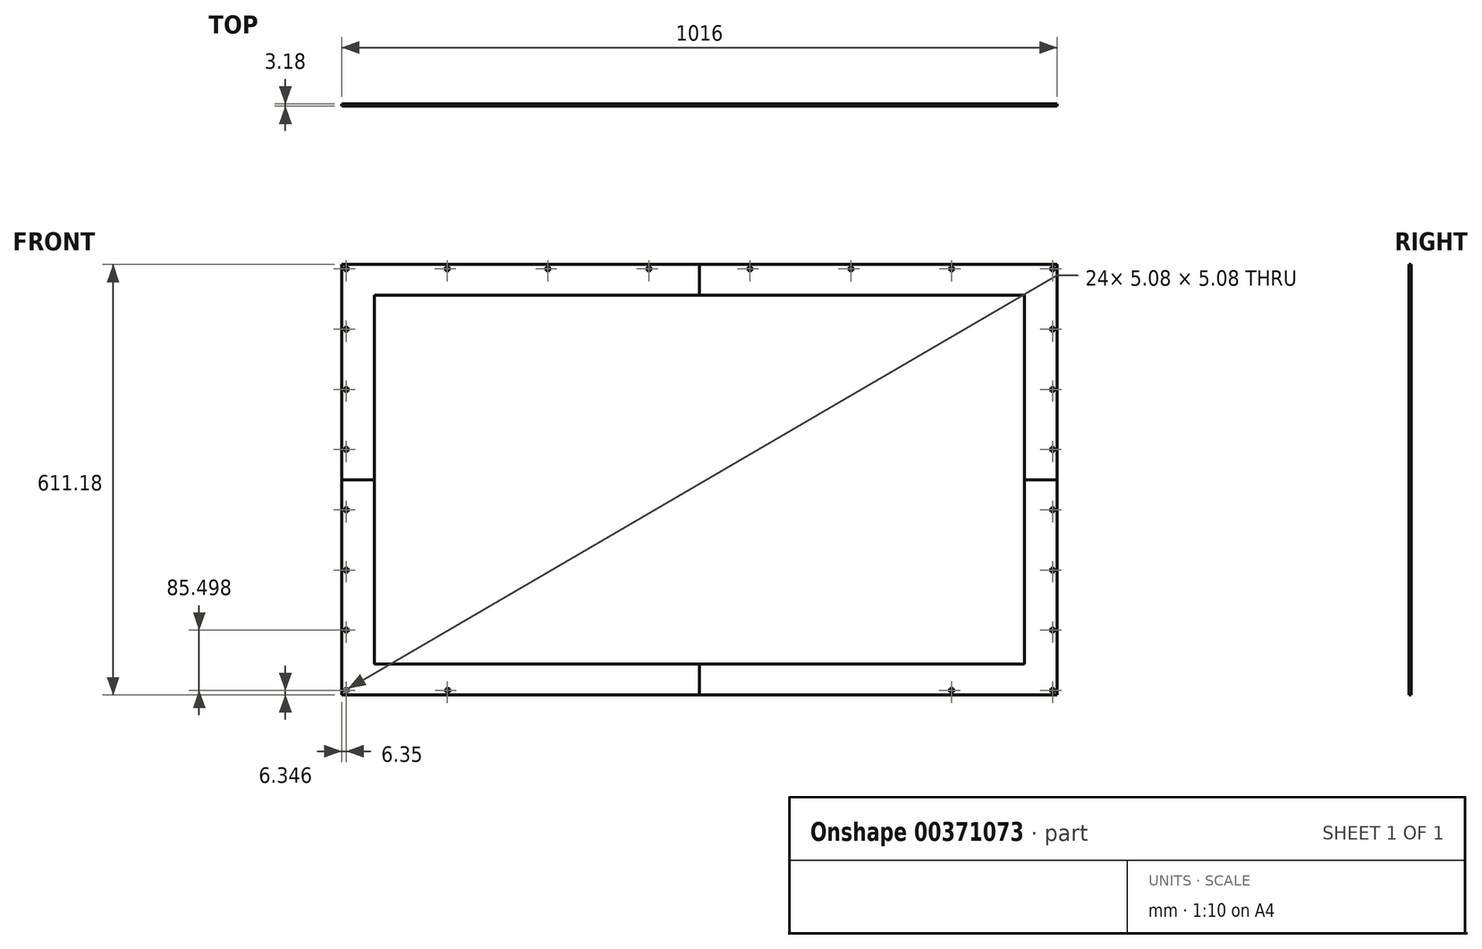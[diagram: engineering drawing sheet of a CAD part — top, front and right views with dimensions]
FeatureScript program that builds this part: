
annotation { "Feature Type Name" : "Feature", "Feature Type Description" : "" }
export const myFeature = defineFeature(function(context is Context, id is Id, definition is map)
    precondition{}
    {
        {
            var Q0;
            Q0=qCreatedBy(makeId("Front.planeOp"),FACE);
            var sketch = newSketch(context, id + "F0", { "sketchPlane" : qUnion([Q0])});
            skLineSegment(sketch, "E0.bottom", {"start": v(495.3, 292.9) * mm, "end": v(-495.3, 292.9) * mm});
            skLineSegment(sketch, "E0.top", {"start": v(495.3, -292.9) * mm, "end": v(-495.3, -292.9) * mm});
            skLineSegment(sketch, "E0.left", {"start": v(495.3, 292.9) * mm, "end": v(495.3, -292.9) * mm});
            skLineSegment(sketch, "E0.right", {"start": v(-495.3, 292.9) * mm, "end": v(-495.3, -292.9) * mm});
            skPoint(sketch, "E0.middle", {"position": v(0, 0) * mm});
            skLineSegment(sketch, "E1.0", {"start": v(-508, 305.6) * mm, "end": v(-508, -305.6) * mm});
            skLineSegment(sketch, "E1.1", {"start": v(508, 305.6) * mm, "end": v(-508, 305.6) * mm});
            skLineSegment(sketch, "E1.2", {"start": v(508, 305.6) * mm, "end": v(508, -305.6) * mm});
            skLineSegment(sketch, "E1.3", {"start": v(508, -305.6) * mm, "end": v(-508, -305.6) * mm});
            skLineSegment(sketch, "E2.bottom", {"start": v(-476, 276.23) * mm, "end": v(476, 276.23) * mm});
            skLineSegment(sketch, "E2.top", {"start": v(-476, -276.23) * mm, "end": v(476, -276.23) * mm});
            skLineSegment(sketch, "E2.left", {"start": v(-476, 276.23) * mm, "end": v(-476, -276.23) * mm});
            skLineSegment(sketch, "E2.right", {"start": v(476, 276.22) * mm, "end": v(476, -276.23) * mm});
            skLineSegment(sketch, "E3.bottom", {"start": v(-355.3, -296.7) * mm, "end": v(-360.38, -296.7) * mm});
            skLineSegment(sketch, "E3.top", {"start": v(-355.3, -301.78) * mm, "end": v(-360.38, -301.78) * mm});
            skLineSegment(sketch, "E3.left", {"start": v(-355.3, -296.7) * mm, "end": v(-355.3, -301.78) * mm});
            skLineSegment(sketch, "E3.right", {"start": v(-360.38, -296.7) * mm, "end": v(-360.38, -301.78) * mm});
            skPoint(sketch, "E3.middle", {"position": v(-357.84, -299.24) * mm});
            skLineSegment(sketch, "E4.MirrorCS", {"start": v(360.38, -296.7) * mm, "end": v(360.38, -301.78) * mm});
            skLineSegment(sketch, "E5.MirrorCS", {"start": v(355.3, -296.7) * mm, "end": v(360.38, -296.7) * mm});
            skLineSegment(sketch, "E6.MirrorCS", {"start": v(355.3, -296.7) * mm, "end": v(355.3, -301.78) * mm});
            skLineSegment(sketch, "E7.MirrorCS", {"start": v(355.3, -301.78) * mm, "end": v(360.38, -301.78) * mm});
            skLineSegment(sketch, "E8.bottom", {"start": v(461.7, 261.93) * mm, "end": v(-461.7, 261.93) * mm});
            skLineSegment(sketch, "E8.top", {"start": v(461.7, -261.93) * mm, "end": v(-461.7, -261.93) * mm});
            skLineSegment(sketch, "E8.left", {"start": v(461.7, 261.93) * mm, "end": v(461.7, -261.93) * mm});
            skLineSegment(sketch, "E8.right", {"start": v(-461.7, 261.93) * mm, "end": v(-461.7, -261.93) * mm});
            skLineSegment(sketch, "E9", {"start": v(-495.3, 292.9) * mm, "end": v(-508, 305.6) * mm});
            skPoint(sketch, "E10", {"position": v(-501.65, 299.24) * mm});
            skLineSegment(sketch, "E11", {"start": v(-495.3, -292.9) * mm, "end": v(-508, -305.6) * mm});
            skPoint(sketch, "E12", {"position": v(-501.65, -299.24) * mm});
            skLineSegment(sketch, "E13", {"start": v(495.3, -292.9) * mm, "end": v(508, -305.6) * mm});
            skPoint(sketch, "E14", {"position": v(501.65, -299.24) * mm});
            skLineSegment(sketch, "E15", {"start": v(495.3, 292.9) * mm, "end": v(508, 305.6) * mm});
            skPoint(sketch, "E16", {"position": v(501.65, 299.24) * mm});
            skPoint(sketch, "E17", {"position": v(-501.65, 213.75) * mm});
            skPoint(sketch, "E18", {"position": v(-501.65, 128.25) * mm});
            skPoint(sketch, "E19", {"position": v(-501.65, 42.75) * mm});
            skPoint(sketch, "E20", {"position": v(-501.65, -42.75) * mm});
            skPoint(sketch, "E21", {"position": v(-501.65, -128.25) * mm});
            skPoint(sketch, "E22", {"position": v(-501.65, -213.75) * mm});
            skLineSegment(sketch, "E23", {"start": v(-501.65, 299.24) * mm, "end": v(-501.65, 213.75) * mm});
            skLineSegment(sketch, "E24", {"start": v(-501.65, 213.75) * mm, "end": v(-501.65, 128.25) * mm});
            skLineSegment(sketch, "E25", {"start": v(-501.65, 128.25) * mm, "end": v(-501.65, 42.75) * mm});
            skLineSegment(sketch, "E26", {"start": v(-501.65, 42.75) * mm, "end": v(-501.65, -42.75) * mm});
            skLineSegment(sketch, "E27", {"start": v(-501.65, -42.75) * mm, "end": v(-501.65, -128.25) * mm});
            skLineSegment(sketch, "E28", {"start": v(-501.65, -128.25) * mm, "end": v(-501.65, -213.75) * mm});
            skLineSegment(sketch, "E29", {"start": v(-501.65, -213.75) * mm, "end": v(-501.65, -299.24) * mm});
            skLineSegment(sketch, "E30.bottom", {"start": v(-499.11, 301.78) * mm, "end": v(-504.2, 301.78) * mm});
            skLineSegment(sketch, "E30.top", {"start": v(-499.11, 296.7) * mm, "end": v(-504.2, 296.7) * mm});
            skLineSegment(sketch, "E30.left", {"start": v(-499.11, 301.78) * mm, "end": v(-499.11, 296.7) * mm});
            skLineSegment(sketch, "E30.right", {"start": v(-504.2, 301.78) * mm, "end": v(-504.2, 296.7) * mm});
            skLineSegment(sketch, "E31.bottom", {"start": v(-499.11, 216.29) * mm, "end": v(-504.2, 216.29) * mm});
            skLineSegment(sketch, "E31.top", {"start": v(-499.11, 211.2) * mm, "end": v(-504.2, 211.2) * mm});
            skLineSegment(sketch, "E31.left", {"start": v(-499.11, 216.29) * mm, "end": v(-499.11, 211.2) * mm});
            skLineSegment(sketch, "E31.right", {"start": v(-504.2, 216.29) * mm, "end": v(-504.2, 211.2) * mm});
            skLineSegment(sketch, "E32.bottom", {"start": v(-499.11, 130.79) * mm, "end": v(-504.2, 130.79) * mm});
            skLineSegment(sketch, "E32.top", {"start": v(-499.11, 125.7) * mm, "end": v(-504.2, 125.7) * mm});
            skLineSegment(sketch, "E32.left", {"start": v(-499.11, 130.79) * mm, "end": v(-499.11, 125.7) * mm});
            skLineSegment(sketch, "E32.right", {"start": v(-504.2, 130.79) * mm, "end": v(-504.2, 125.7) * mm});
            skLineSegment(sketch, "E33.bottom", {"start": v(-499.11, 45.29) * mm, "end": v(-504.2, 45.29) * mm});
            skLineSegment(sketch, "E33.top", {"start": v(-499.11, 40.2) * mm, "end": v(-504.2, 40.2) * mm});
            skLineSegment(sketch, "E33.left", {"start": v(-499.11, 45.29) * mm, "end": v(-499.11, 40.2) * mm});
            skLineSegment(sketch, "E33.right", {"start": v(-504.2, 45.29) * mm, "end": v(-504.2, 40.2) * mm});
            skLineSegment(sketch, "E34.bottom", {"start": v(-499.1, -40.2) * mm, "end": v(-504.19, -40.2) * mm});
            skLineSegment(sketch, "E34.top", {"start": v(-499.1, -45.29) * mm, "end": v(-504.19, -45.29) * mm});
            skLineSegment(sketch, "E34.left", {"start": v(-499.1, -40.2) * mm, "end": v(-499.1, -45.29) * mm});
            skLineSegment(sketch, "E34.right", {"start": v(-504.19, -40.2) * mm, "end": v(-504.19, -45.29) * mm});
            skLineSegment(sketch, "E35.bottom", {"start": v(-499.1, -125.7) * mm, "end": v(-504.19, -125.7) * mm});
            skLineSegment(sketch, "E35.top", {"start": v(-499.1, -130.79) * mm, "end": v(-504.19, -130.79) * mm});
            skLineSegment(sketch, "E35.left", {"start": v(-499.1, -125.7) * mm, "end": v(-499.1, -130.79) * mm});
            skLineSegment(sketch, "E35.right", {"start": v(-504.19, -125.7) * mm, "end": v(-504.19, -130.79) * mm});
            skLineSegment(sketch, "E36.bottom", {"start": v(-499.1, -211.2) * mm, "end": v(-504.19, -211.2) * mm});
            skLineSegment(sketch, "E36.top", {"start": v(-499.1, -216.29) * mm, "end": v(-504.19, -216.29) * mm});
            skLineSegment(sketch, "E36.left", {"start": v(-499.1, -211.2) * mm, "end": v(-499.1, -216.29) * mm});
            skLineSegment(sketch, "E36.right", {"start": v(-504.19, -211.2) * mm, "end": v(-504.19, -216.29) * mm});
            skLineSegment(sketch, "E37.bottom", {"start": v(-499.11, -301.78) * mm, "end": v(-504.2, -301.78) * mm});
            skLineSegment(sketch, "E37.top", {"start": v(-499.11, -296.7) * mm, "end": v(-504.2, -296.7) * mm});
            skLineSegment(sketch, "E37.left", {"start": v(-499.11, -301.78) * mm, "end": v(-499.11, -296.7) * mm});
            skLineSegment(sketch, "E37.right", {"start": v(-504.2, -301.78) * mm, "end": v(-504.2, -296.7) * mm});
            skLineSegment(sketch, "E38.MirrorCS", {"start": v(499.11, 301.78) * mm, "end": v(504.2, 301.78) * mm});
            skLineSegment(sketch, "E39.MirrorCS", {"start": v(504.2, 301.78) * mm, "end": v(504.2, 296.7) * mm});
            skLineSegment(sketch, "E40.MirrorCS", {"start": v(499.11, 296.7) * mm, "end": v(504.2, 296.7) * mm});
            skLineSegment(sketch, "E41.MirrorCS", {"start": v(499.11, 301.78) * mm, "end": v(499.11, 296.7) * mm});
            skLineSegment(sketch, "E42.MirrorCS", {"start": v(499.11, 216.29) * mm, "end": v(504.2, 216.29) * mm});
            skLineSegment(sketch, "E43.MirrorCS", {"start": v(499.11, 216.29) * mm, "end": v(499.11, 211.2) * mm});
            skLineSegment(sketch, "E44.MirrorCS", {"start": v(499.11, 211.2) * mm, "end": v(504.2, 211.2) * mm});
            skLineSegment(sketch, "E45.MirrorCS", {"start": v(504.2, 216.29) * mm, "end": v(504.2, 211.2) * mm});
            skPoint(sketch, "E46.MirrorP", {"position": v(501.65, 213.75) * mm});
            skLineSegment(sketch, "E47.MirrorCS", {"start": v(499.11, 130.79) * mm, "end": v(504.2, 130.79) * mm});
            skLineSegment(sketch, "E48.MirrorCS", {"start": v(499.11, 130.79) * mm, "end": v(499.11, 125.7) * mm});
            skLineSegment(sketch, "E49.MirrorCS", {"start": v(499.11, 125.7) * mm, "end": v(504.2, 125.7) * mm});
            skLineSegment(sketch, "E50.MirrorCS", {"start": v(504.2, 130.79) * mm, "end": v(504.2, 125.7) * mm});
            skPoint(sketch, "E51.MirrorP", {"position": v(501.65, 128.25) * mm});
            skLineSegment(sketch, "E52.MirrorCS", {"start": v(499.11, 45.29) * mm, "end": v(504.2, 45.29) * mm});
            skLineSegment(sketch, "E53.MirrorCS", {"start": v(499.11, 45.29) * mm, "end": v(499.11, 40.2) * mm});
            skLineSegment(sketch, "E54.MirrorCS", {"start": v(499.11, 40.2) * mm, "end": v(504.2, 40.2) * mm});
            skLineSegment(sketch, "E55.MirrorCS", {"start": v(504.2, 45.29) * mm, "end": v(504.2, 40.2) * mm});
            skPoint(sketch, "E56.MirrorP", {"position": v(501.65, 42.75) * mm});
            skLineSegment(sketch, "E57.MirrorCS", {"start": v(499.1, -40.2) * mm, "end": v(504.19, -40.2) * mm});
            skLineSegment(sketch, "E58.MirrorCS", {"start": v(499.1, -40.2) * mm, "end": v(499.1, -45.29) * mm});
            skLineSegment(sketch, "E59.MirrorCS", {"start": v(499.1, -45.29) * mm, "end": v(504.19, -45.29) * mm});
            skLineSegment(sketch, "E60.MirrorCS", {"start": v(504.19, -40.2) * mm, "end": v(504.19, -45.29) * mm});
            skPoint(sketch, "E61.MirrorP", {"position": v(501.65, -42.75) * mm});
            skLineSegment(sketch, "E62.MirrorCS", {"start": v(499.1, -125.7) * mm, "end": v(504.19, -125.7) * mm});
            skLineSegment(sketch, "E63.MirrorCS", {"start": v(499.1, -125.7) * mm, "end": v(499.1, -130.79) * mm});
            skLineSegment(sketch, "E64.MirrorCS", {"start": v(499.1, -130.79) * mm, "end": v(504.19, -130.79) * mm});
            skLineSegment(sketch, "E65.MirrorCS", {"start": v(504.19, -125.7) * mm, "end": v(504.19, -130.79) * mm});
            skPoint(sketch, "E66.MirrorP", {"position": v(501.65, -128.25) * mm});
            skLineSegment(sketch, "E67.MirrorCS", {"start": v(499.1, -211.2) * mm, "end": v(504.19, -211.2) * mm});
            skLineSegment(sketch, "E68.MirrorCS", {"start": v(499.1, -211.2) * mm, "end": v(499.1, -216.29) * mm});
            skLineSegment(sketch, "E69.MirrorCS", {"start": v(499.1, -216.29) * mm, "end": v(504.19, -216.29) * mm});
            skLineSegment(sketch, "E70.MirrorCS", {"start": v(504.19, -211.2) * mm, "end": v(504.19, -216.29) * mm});
            skPoint(sketch, "E71.MirrorP", {"position": v(501.65, -213.75) * mm});
            skLineSegment(sketch, "E72.MirrorCS", {"start": v(499.11, -296.7) * mm, "end": v(504.2, -296.7) * mm});
            skLineSegment(sketch, "E73.MirrorCS", {"start": v(499.11, -301.78) * mm, "end": v(499.11, -296.7) * mm});
            skLineSegment(sketch, "E74.MirrorCS", {"start": v(499.11, -301.78) * mm, "end": v(504.2, -301.78) * mm});
            skLineSegment(sketch, "E75.MirrorCS", {"start": v(504.2, -301.78) * mm, "end": v(504.2, -296.7) * mm});
            skPoint(sketch, "E76", {"position": v(-358.32, 299.24) * mm});
            skPoint(sketch, "E77", {"position": v(-215, 299.24) * mm});
            skPoint(sketch, "E78", {"position": v(-71.66, 299.24) * mm});
            skPoint(sketch, "E79", {"position": v(71.66, 299.24) * mm});
            skPoint(sketch, "E80", {"position": v(215, 299.24) * mm});
            skPoint(sketch, "E81", {"position": v(358.32, 299.24) * mm});
            skLineSegment(sketch, "E82.bottom", {"start": v(-355.78, 301.78) * mm, "end": v(-360.86, 301.78) * mm});
            skLineSegment(sketch, "E82.top", {"start": v(-355.78, 296.7) * mm, "end": v(-360.86, 296.7) * mm});
            skLineSegment(sketch, "E82.left", {"start": v(-355.78, 301.78) * mm, "end": v(-355.78, 296.7) * mm});
            skLineSegment(sketch, "E82.right", {"start": v(-360.86, 301.78) * mm, "end": v(-360.86, 296.7) * mm});
            skLineSegment(sketch, "E83.bottom", {"start": v(-212.45, 301.78) * mm, "end": v(-217.53, 301.78) * mm});
            skLineSegment(sketch, "E83.top", {"start": v(-212.45, 296.7) * mm, "end": v(-217.53, 296.7) * mm});
            skLineSegment(sketch, "E83.left", {"start": v(-212.45, 301.78) * mm, "end": v(-212.45, 296.7) * mm});
            skLineSegment(sketch, "E83.right", {"start": v(-217.53, 301.78) * mm, "end": v(-217.53, 296.7) * mm});
            skLineSegment(sketch, "E84.bottom", {"start": v(-69.12, 301.78) * mm, "end": v(-74.2, 301.78) * mm});
            skLineSegment(sketch, "E84.top", {"start": v(-69.12, 296.7) * mm, "end": v(-74.2, 296.7) * mm});
            skLineSegment(sketch, "E84.left", {"start": v(-69.12, 301.78) * mm, "end": v(-69.12, 296.7) * mm});
            skLineSegment(sketch, "E84.right", {"start": v(-74.2, 301.78) * mm, "end": v(-74.2, 296.7) * mm});
            skLineSegment(sketch, "E85.bottom", {"start": v(74.2, 301.78) * mm, "end": v(69.12, 301.78) * mm});
            skLineSegment(sketch, "E85.top", {"start": v(74.2, 296.7) * mm, "end": v(69.12, 296.7) * mm});
            skLineSegment(sketch, "E85.left", {"start": v(74.2, 301.78) * mm, "end": v(74.2, 296.7) * mm});
            skLineSegment(sketch, "E85.right", {"start": v(69.12, 301.78) * mm, "end": v(69.12, 296.7) * mm});
            skLineSegment(sketch, "E86.bottom", {"start": v(217.53, 301.78) * mm, "end": v(212.45, 301.78) * mm});
            skLineSegment(sketch, "E86.top", {"start": v(217.53, 296.7) * mm, "end": v(212.45, 296.7) * mm});
            skLineSegment(sketch, "E86.left", {"start": v(217.53, 301.78) * mm, "end": v(217.53, 296.7) * mm});
            skLineSegment(sketch, "E86.right", {"start": v(212.45, 301.78) * mm, "end": v(212.45, 296.7) * mm});
            skLineSegment(sketch, "E87.bottom", {"start": v(360.86, 301.78) * mm, "end": v(355.78, 301.78) * mm});
            skLineSegment(sketch, "E87.top", {"start": v(360.86, 296.7) * mm, "end": v(355.78, 296.7) * mm});
            skLineSegment(sketch, "E87.left", {"start": v(360.86, 301.78) * mm, "end": v(360.86, 296.7) * mm});
            skLineSegment(sketch, "E87.right", {"start": v(355.78, 301.78) * mm, "end": v(355.78, 296.7) * mm});
            skLineSegment(sketch, "E88", {"start": v(-501.65, 299.24) * mm, "end": v(-358.32, 299.24) * mm});
            skLineSegment(sketch, "E89", {"start": v(-358.32, 299.24) * mm, "end": v(-215, 299.24) * mm});
            skLineSegment(sketch, "E90", {"start": v(-215, 299.24) * mm, "end": v(-71.66, 299.24) * mm});
            skLineSegment(sketch, "E91", {"start": v(-71.66, 299.24) * mm, "end": v(71.66, 299.24) * mm});
            skLineSegment(sketch, "E92", {"start": v(71.66, 299.24) * mm, "end": v(215, 299.24) * mm});
            skLineSegment(sketch, "E93", {"start": v(215, 299.24) * mm, "end": v(358.32, 299.24) * mm});
            skLineSegment(sketch, "E94", {"start": v(358.32, 299.24) * mm, "end": v(501.65, 299.24) * mm});
            skPoint(sketch, "E95", {"position": v(357.84, -299.24) * mm});
            skPoint(sketch, "E95.positionSnap0", {"position": v(360.38, -299.24) * mm});
            skPoint(sketch, "E95.positionSnap1", {"position": v(357.84, -296.7) * mm});
            skLineSegment(sketch, "E96", {"start": v(0, 261.93) * mm, "end": v(0, 305.6) * mm});
            skLineSegment(sketch, "E97", {"start": v(-461.7, 0) * mm, "end": v(-508, 0) * mm});
            skLineSegment(sketch, "E98", {"start": v(0, -261.93) * mm, "end": v(0, -305.6) * mm});
            skLineSegment(sketch, "E99", {"start": v(461.7, 0) * mm, "end": v(508, 0) * mm});
            skSolve(sketch);
        }
        {
            var Q0;
            {var subQ4=sQuery(id+"F0.wireOp",EDGE,"E30.right");Q0=makeQuery(id+"F0.imprint","IMPRINT",FACE,{"disambiguationData":[TD([[makeQuery(id+"F0.imprint","IMPRINT",EDGE,{"derivedFrom":subQ4}),-1.0]])]});}
            var Q1;
            {var subQ0=sQuery(id+"F0.wireOp",EDGE,"E31.left");Q1=makeQuery(id+"F0.imprint","IMPRINT",FACE,{"disambiguationData":[TD([[makeQuery(id+"F0.imprint","IMPRINT",EDGE,{"derivedFrom":subQ0}),1.0]])]});}
            var Q2;
            {var subQ5=sQuery(id+"F0.wireOp",EDGE,"E2.left");var subQ6=sQuery(id+"F0.wireOp",EDGE,"E2.bottom");var subQ7=makeQuery(id+"F0.imprint","INTERSECT",VERTEX,{"derivedFrom":[subQ6,subQ5]});Q2=makeQuery(id+"F0.imprint","IMPRINT",FACE,{"disambiguationData":[TD([[makeQuery(id+"F0.imprint","IMPRINT",EDGE,{"disambiguationData":[TD([[subQ7,-1.0]])],"derivedFrom":subQ6}),-1.0]])]});}
            var Q3;
            {var subQ6=sQuery(id+"F0.wireOp",EDGE,"E82.top");Q3=makeQuery(id+"F0.imprint","IMPRINT",FACE,{"disambiguationData":[TD([[makeQuery(id+"F0.imprint","IMPRINT",EDGE,{"derivedFrom":subQ6}),1.0]])]});}
            var Q4;
            {var subQ13=sQuery(id+"F0.wireOp",EDGE,"E30.bottom");Q4=makeQuery(id+"F0.imprint","IMPRINT",FACE,{"disambiguationData":[TD([[makeQuery(id+"F0.imprint","IMPRINT",EDGE,{"derivedFrom":subQ13}),-1.0]])]});}
            var Q5;
            {var subQ0=sQuery(id+"F0.wireOp",EDGE,"E2.left");var subQ1=sQuery(id+"F0.wireOp",EDGE,"E2.bottom");var subQ2=makeQuery(id+"F0.imprint","INTERSECT",VERTEX,{"derivedFrom":[subQ1,subQ0]});Q5=makeQuery(id+"F0.imprint","IMPRINT",FACE,{"disambiguationData":[TD([[makeQuery(id+"F0.imprint","IMPRINT",EDGE,{"disambiguationData":[TD([[subQ2,-1.0]])],"derivedFrom":subQ1}),1.0]])]});}
            extrude(context, id + "F1", {"entities" : qUnion([Q0, Q1, Q2, Q3, Q4, Q5]), "endBound" : BoundingType.SYMMETRIC, "oppositeDirection" : true, "depth" : 3.17 * mm});
        }
        {
            var Q0;
            {var subQ19=sQuery(id+"F0.wireOp",EDGE,"E38.MirrorCS");Q0=makeQuery(id+"F0.imprint","IMPRINT",FACE,{"disambiguationData":[TD([[makeQuery(id+"F0.imprint","IMPRINT",EDGE,{"derivedFrom":subQ19}),1.0]])]});}
            var Q1;
            {var subQ16=sQuery(id+"F0.wireOp",EDGE,"E85.top");Q1=makeQuery(id+"F0.imprint","IMPRINT",FACE,{"disambiguationData":[TD([[makeQuery(id+"F0.imprint","IMPRINT",EDGE,{"derivedFrom":subQ16}),1.0]])]});}
            var Q2;
            {var subQ0=sQuery(id+"F0.wireOp",EDGE,"E2.right");var subQ1=sQuery(id+"F0.wireOp",EDGE,"E2.bottom");var subQ2=makeQuery(id+"F0.imprint","INTERSECT",VERTEX,{"derivedFrom":[subQ1,subQ0]});Q2=makeQuery(id+"F0.imprint","IMPRINT",FACE,{"disambiguationData":[TD([[makeQuery(id+"F0.imprint","IMPRINT",EDGE,{"disambiguationData":[TD([[subQ2,1.0]])],"derivedFrom":subQ1}),1.0]])]});}
            var Q3;
            {var subQ7=sQuery(id+"F0.wireOp",EDGE,"E2.right");var subQ8=sQuery(id+"F0.wireOp",EDGE,"E2.bottom");var subQ9=makeQuery(id+"F0.imprint","INTERSECT",VERTEX,{"derivedFrom":[subQ8,subQ7]});Q3=makeQuery(id+"F0.imprint","IMPRINT",FACE,{"disambiguationData":[TD([[makeQuery(id+"F0.imprint","IMPRINT",EDGE,{"disambiguationData":[TD([[subQ9,1.0]])],"derivedFrom":subQ8}),-1.0]])]});}
            var Q4;
            {var subQ1=sQuery(id+"F0.wireOp",EDGE,"E39.MirrorCS");Q4=makeQuery(id+"F0.imprint","IMPRINT",FACE,{"disambiguationData":[TD([[makeQuery(id+"F0.imprint","IMPRINT",EDGE,{"derivedFrom":subQ1}),1.0]])]});}
            extrude(context, id + "F2", {"entities" : qUnion([Q0, Q1, Q2, Q3, Q4]), "endBound" : BoundingType.SYMMETRIC, "depth" : 3.17 * mm});
        }
        {
            var Q0;
            Q0=makeQuery(id+"F0.imprint","IMPRINT",FACE,{"disambiguationData":[TD([[makeQuery(id+"F0.imprint","IMPRINT",EDGE,{"derivedFrom":sQuery(id+"F0.wireOp",EDGE,"E57.MirrorCS")}),1.0]])]});
            var Q1;
            {var subQ0=sQuery(id+"F0.wireOp",EDGE,"E2.right");var subQ1=sQuery(id+"F0.wireOp",EDGE,"E2.top");var subQ2=makeQuery(id+"F0.imprint","INTERSECT",VERTEX,{"derivedFrom":[subQ1,subQ0]});Q1=makeQuery(id+"F0.imprint","IMPRINT",FACE,{"disambiguationData":[TD([[makeQuery(id+"F0.imprint","IMPRINT",EDGE,{"disambiguationData":[TD([[subQ2,1.0]])],"derivedFrom":subQ1}),-1.0]])]});}
            var Q2;
            {var subQ5=sQuery(id+"F0.wireOp",EDGE,"E2.right");var subQ6=sQuery(id+"F0.wireOp",EDGE,"E2.top");var subQ7=makeQuery(id+"F0.imprint","INTERSECT",VERTEX,{"derivedFrom":[subQ6,subQ5]});Q2=makeQuery(id+"F0.imprint","IMPRINT",FACE,{"disambiguationData":[TD([[makeQuery(id+"F0.imprint","IMPRINT",EDGE,{"disambiguationData":[TD([[subQ7,1.0]])],"derivedFrom":subQ6}),1.0]])]});}
            var Q3;
            Q3=makeQuery(id+"F0.imprint","IMPRINT",FACE,{"disambiguationData":[TD([[makeQuery(id+"F0.imprint","IMPRINT",EDGE,{"derivedFrom":sQuery(id+"F0.wireOp",EDGE,"E4.MirrorCS")}),1.0]])]});
            extrude(context, id + "F3", {"entities" : qUnion([Q0, Q1, Q2, Q3]), "endBound" : BoundingType.SYMMETRIC, "depth" : 3.17 * mm});
        }
        {
            var Q0;
            Q0=makeQuery(id+"F0.imprint","IMPRINT",FACE,{"disambiguationData":[TD([[makeQuery(id+"F0.imprint","IMPRINT",EDGE,{"derivedFrom":sQuery(id+"F0.wireOp",EDGE,"E3.bottom")}),-1.0]])]});
            var Q1;
            {var subQ0=sQuery(id+"F0.wireOp",EDGE,"E2.left");var subQ1=sQuery(id+"F0.wireOp",EDGE,"E2.top");var subQ2=makeQuery(id+"F0.imprint","INTERSECT",VERTEX,{"derivedFrom":[subQ1,subQ0]});Q1=makeQuery(id+"F0.imprint","IMPRINT",FACE,{"disambiguationData":[TD([[makeQuery(id+"F0.imprint","IMPRINT",EDGE,{"disambiguationData":[TD([[subQ2,-1.0]])],"derivedFrom":subQ1}),-1.0]])]});}
            var Q2;
            {var subQ7=sQuery(id+"F0.wireOp",EDGE,"E2.left");var subQ8=sQuery(id+"F0.wireOp",EDGE,"E2.top");var subQ9=makeQuery(id+"F0.imprint","INTERSECT",VERTEX,{"derivedFrom":[subQ8,subQ7]});Q2=makeQuery(id+"F0.imprint","IMPRINT",FACE,{"disambiguationData":[TD([[makeQuery(id+"F0.imprint","IMPRINT",EDGE,{"disambiguationData":[TD([[subQ9,-1.0]])],"derivedFrom":subQ8}),1.0]])]});}
            var Q3;
            {var subQ4=sQuery(id+"F0.wireOp",EDGE,"E34.left");Q3=makeQuery(id+"F0.imprint","IMPRINT",FACE,{"disambiguationData":[TD([[makeQuery(id+"F0.imprint","IMPRINT",EDGE,{"derivedFrom":subQ4}),1.0]])]});}
            var Q4;
            {var subQ0=sQuery(id+"F0.wireOp",EDGE,"E34.right");Q4=makeQuery(id+"F0.imprint","IMPRINT",FACE,{"disambiguationData":[TD([[makeQuery(id+"F0.imprint","IMPRINT",EDGE,{"derivedFrom":subQ0}),-1.0]])]});}
            extrude(context, id + "F4", {"entities" : qUnion([Q0, Q1, Q2, Q3, Q4]), "endBound" : BoundingType.SYMMETRIC, "depth" : 3.17 * mm});
        }
    });
